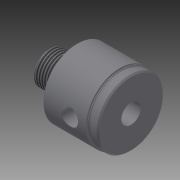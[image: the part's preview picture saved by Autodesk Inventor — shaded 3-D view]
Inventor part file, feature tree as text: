
AUTODESK INVENTOR PART (.ipt)
format: ipt  version: 2014 (Build 180170000, 170)  size: 258,560 bytes
history: native  units: in
note: dims shown in document units (in); Inventor stores cm internally (conversion verified against a paired STEP export)
features: other x112, sketch x5, revolve x4, thread x1, hole x1
ambient origin geometry x8: Origin, YZ Plane, XZ Plane, XY Plane, X Axis, Y Axis, Z Axis, Center Point
bodies: Solid1 (feature_tree)
feature tree (123):
  revolve  "Revolution1"  [1 undecoded]
  thread  "Thread1"  [1 undecoded]
  revolve  "Revolution2"  Angle=360.0deg
  hole  "Hole1"  [1 undecoded]
  revolve  "Revolution3"  [1 undecoded]
  revolve  "Revolution4"  [1 undecoded]
  other  "dp1_XY"
  other  "dp1_YZ"
  other  "dp1_ZX"
  other  "dp1_X"
  other  "dp1_Y"
  other  "dp1_Z"
  other  "dp1_Center"
  other  "dp2_XY"
  other  "dp2_YZ"
  other  "dp2_ZX"
  other  "dp2_X"
  other  "dp2_Y"
  other  "dp2_Z"
  other  "dp2_Center"
  other  "port_XY"
  other  "port_YZ"
  other  "port_ZX"
  other  "port_X"
  other  "port_Y"
  other  "port_Z"
  other  "port_Center"
  other  "rod_guide_XY"
  other  "rod_guide_YZ"
  other  "rod_guide_ZX"
  other  "rod_guide_X"
  other  "rod_guide_Y"
  other  "rod_guide_Z"
  other  "rod_guide_Center"
  other  "s1_XY"
  other  "s1_YZ"
  other  "s1_ZX"
  other  "s1_X"
  other  "s1_Y"
  other  "s1_Z"
  other  "s1_Center"
  other  "s2_XY"
  other  "s2_YZ"
  other  "s2_ZX"
  other  "s2_X"
  other  "s2_Y"
  other  "s2_Z"
  other  "s2_Center"
  other  "t1_XY"
  other  "t1_YZ"
  other  "t1_ZX"
  other  "t1_X"
  other  "t1_Y"
  other  "t1_Z"
  other  "t1_Center"
  other  "t111_XY"
  other  "t111_YZ"
  other  "t111_ZX"
  other  "t111_X"
  other  "t111_Y"
  other  "t111_Z"
  other  "t111_Center"
  other  "to_foot_bracket_XY"
  other  "to_foot_bracket_YZ"
  other  "to_foot_bracket_ZX"
  other  "to_foot_bracket_X"
  other  "to_foot_bracket_Y"
  other  "to_foot_bracket_Z"
  other  "to_foot_bracket_Center"
  other  "to_nut_XY"
  other  "to_nut_YZ"
  other  "to_nut_ZX"
  other  "to_nut_X"
  other  "to_nut_Y"
  other  "to_nut_Z"
  other  "to_nut_Center"
  other  "to_rod_XY"
  other  "to_rod_YZ"
  other  "to_rod_ZX"
  other  "to_rod_X"
  other  "to_rod_Y"
  other  "to_rod_Z"
  other  "to_rod_Center"
  other  "to_screw_XY"
  other  "to_screw_YZ"
  other  "to_screw_ZX"
  other  "to_screw_X"
  other  "to_screw_Y"
  other  "to_screw_Z"
  other  "to_screw_Center"
  other  "to_trunnion_brackets_XY"
  other  "to_trunnion_brackets_YZ"
  other  "to_trunnion_brackets_ZX"
  other  "to_trunnion_brackets_X"
  other  "to_trunnion_brackets_Y"
  other  "to_trunnion_brackets_Z"
  other  "to_trunnion_brackets_Center"
  other  "to_trunnion_brackets1_XY"
  other  "to_trunnion_brackets1_YZ"
  other  "to_trunnion_brackets1_ZX"
  other  "to_trunnion_brackets1_X"
  other  "to_trunnion_brackets1_Y"
  other  "to_trunnion_brackets1_Z"
  other  "to_trunnion_brackets1_Center"
  other  "to_trunnion_brackets2_XY"
  other  "to_trunnion_brackets2_YZ"
  other  "to_trunnion_brackets2_ZX"
  other  "to_trunnion_brackets2_X"
  other  "to_trunnion_brackets2_Y"
  other  "to_trunnion_brackets2_Z"
  other  "to_trunnion_brackets2_Center"
  other  "to_tube_XY"
  other  "to_tube_YZ"
  other  "to_tube_ZX"
  other  "to_tube_X"
  other  "to_tube_Y"
  other  "to_tube_Z"
  other  "to_tube_Center"
  sketch  "Sketch_2"  dims[d0=360.0deg d1=0.3297in d2=0.0in d3=360.0deg]
  sketch  "Sketch_3"  dims[d4=0.442in d5=0.75in d6=0.502in d7=0.25in d8=90.0deg d9=1.875in d10=0.0in d11=360.0deg]
  sketch  "Sketch3"  dims[d12=360.0deg]
  sketch  "Sketch_40"
  sketch  "Sketch_47"
note: 5 required parameter values undecoded (feature->parameter linkage not recoverable at this tier; creation-order binding heuristic only, values carry confidence <= 0.55)